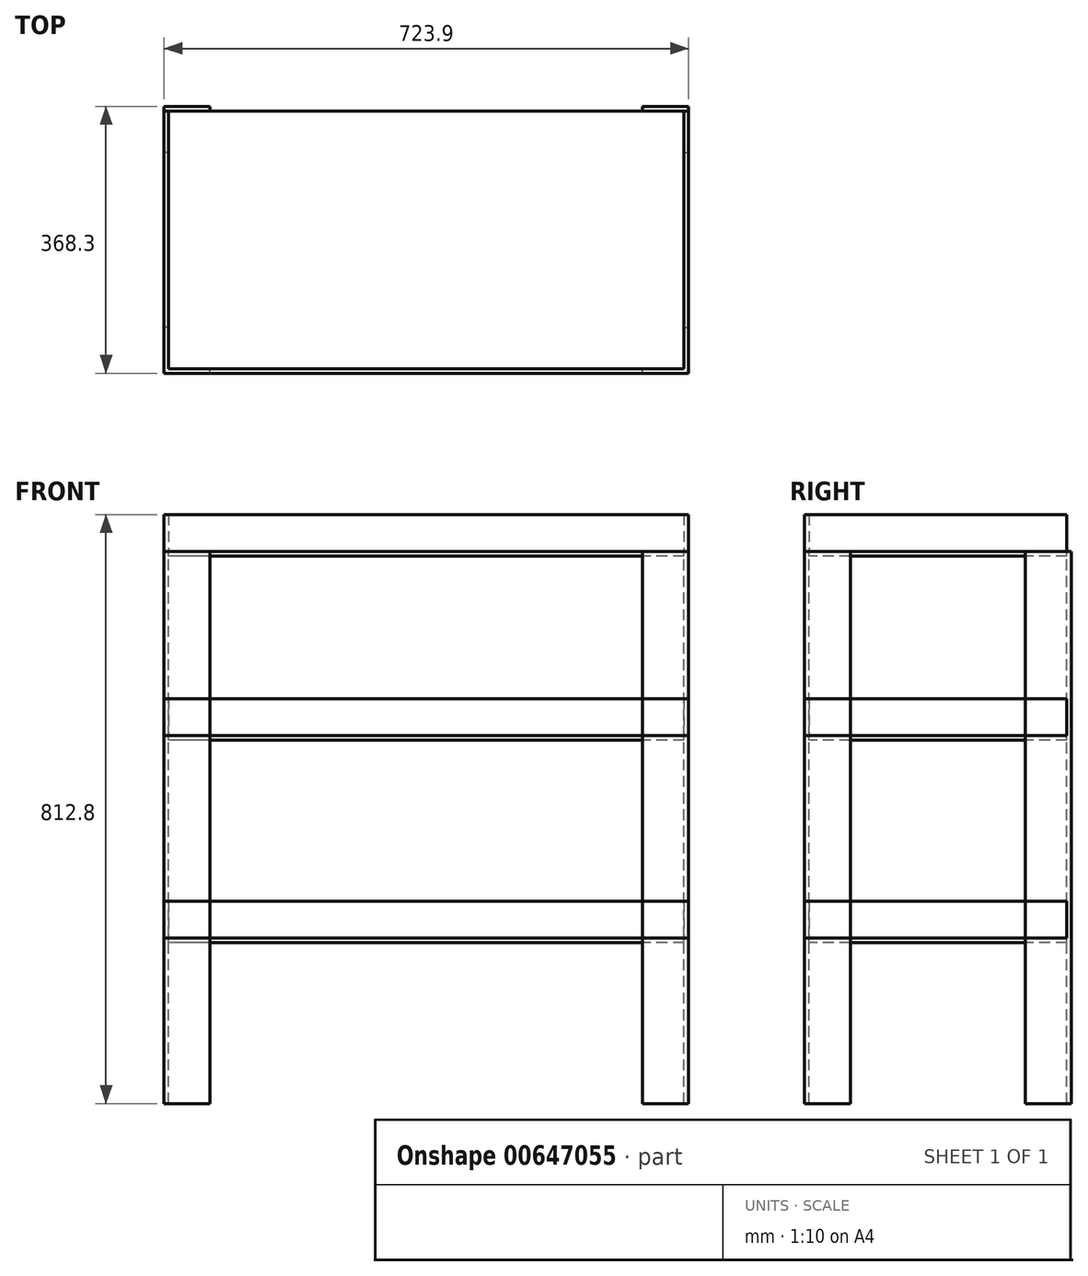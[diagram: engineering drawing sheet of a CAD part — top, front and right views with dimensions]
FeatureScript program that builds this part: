
annotation { "Feature Type Name" : "Feature", "Feature Type Description" : "" }
export const myFeature = defineFeature(function(context is Context, id is Id, definition is map)
    precondition{}
    {
        {
            var Q0;
            Q0=qCreatedBy(makeId("Top.planeOp"),FACE);
            cPlane(context, id + "F0", {"entities" : qUnion([Q0]), "cplaneType" : CPlaneType.OFFSET, "offset" : 152.4 * mm, "width" : 152.4 * mm, "height" : 152.4 * mm});
        }
        {
            var Q0;
            Q0=qCreatedBy(id+"F0.planeOp",FACE);
            cPlane(context, id + "F1", {"entities" : qUnion([Q0]), "cplaneType" : CPlaneType.OFFSET, "offset" : 279.4 * mm, "width" : 152.4 * mm, "height" : 152.4 * mm});
        }
        {
            var Q0;
            Q0=qCreatedBy(id+"F1.planeOp",FACE);
            cPlane(context, id + "F2", {"entities" : qUnion([Q0]), "cplaneType" : CPlaneType.OFFSET, "offset" : 254 * mm, "width" : 152.4 * mm, "height" : 152.4 * mm});
        }
        {
            var Q0;
            Q0=qCreatedBy(id+"F2.planeOp",FACE);
            var sketch = newSketch(context, id + "F3", { "sketchPlane" : qUnion([Q0])});
            skLineSegment(sketch, "E0.bottom", {"start": v(355.6, 177.8) * mm, "end": v(-355.6, 177.8) * mm, "construction": true});
            skLineSegment(sketch, "E0.top", {"start": v(355.6, -177.8) * mm, "end": v(-355.6, -177.8) * mm, "construction": true});
            skLineSegment(sketch, "E0.left", {"start": v(355.6, 177.8) * mm, "end": v(355.6, -177.8) * mm, "construction": true});
            skLineSegment(sketch, "E0.right", {"start": v(-355.6, 177.8) * mm, "end": v(-355.6, -177.8) * mm, "construction": true});
            skPoint(sketch, "E0.middle", {"position": v(0, 0) * mm});
            skLineSegment(sketch, "E1", {"start": v(-355.6, 120.65) * mm, "end": v(-361.95, 120.65) * mm});
            skLineSegment(sketch, "E2", {"start": v(-361.95, 120.65) * mm, "end": v(-361.95, 184.15) * mm});
            skLineSegment(sketch, "E3", {"start": v(-361.95, 184.15) * mm, "end": v(-298.45, 184.15) * mm});
            skLineSegment(sketch, "E4", {"start": v(-298.45, 184.15) * mm, "end": v(-298.45, 177.8) * mm});
            skLineSegment(sketch, "E5", {"start": v(-298.45, 177.8) * mm, "end": v(-355.6, 177.8) * mm});
            skLineSegment(sketch, "E6", {"start": v(-355.6, 120.65) * mm, "end": v(-355.6, 177.8) * mm});
            skLineSegment(sketch, "E7", {"start": v(-355.6, -177.8) * mm, "end": v(-355.6, -120.65) * mm});
            skLineSegment(sketch, "E8", {"start": v(-355.6, -120.65) * mm, "end": v(-361.95, -120.65) * mm});
            skLineSegment(sketch, "E9", {"start": v(-361.95, -184.15) * mm, "end": v(-361.95, -120.65) * mm});
            skLineSegment(sketch, "E10", {"start": v(-361.95, -184.15) * mm, "end": v(-298.45, -184.15) * mm});
            skLineSegment(sketch, "E11", {"start": v(-298.45, -184.15) * mm, "end": v(-298.45, -177.8) * mm});
            skLineSegment(sketch, "E12", {"start": v(-298.45, -177.8) * mm, "end": v(-355.6, -177.8) * mm});
            skLineSegment(sketch, "E13.MirrorCS", {"start": v(361.95, -184.15) * mm, "end": v(298.45, -184.15) * mm});
            skLineSegment(sketch, "E14.MirrorCS", {"start": v(298.45, -177.8) * mm, "end": v(355.6, -177.8) * mm});
            skLineSegment(sketch, "E15.MirrorCS", {"start": v(298.45, -184.15) * mm, "end": v(298.45, -177.8) * mm});
            skLineSegment(sketch, "E16.MirrorCS", {"start": v(355.6, -120.65) * mm, "end": v(361.95, -120.65) * mm});
            skLineSegment(sketch, "E17.MirrorCS", {"start": v(355.6, -177.8) * mm, "end": v(355.6, -120.65) * mm});
            skLineSegment(sketch, "E18.MirrorCS", {"start": v(361.95, -184.15) * mm, "end": v(361.95, -120.65) * mm});
            skLineSegment(sketch, "E19.MirrorCS", {"start": v(355.6, 120.65) * mm, "end": v(355.6, 177.8) * mm});
            skLineSegment(sketch, "E20.MirrorCS", {"start": v(298.45, 177.8) * mm, "end": v(355.6, 177.8) * mm});
            skLineSegment(sketch, "E21.MirrorCS", {"start": v(298.45, 184.15) * mm, "end": v(298.45, 177.8) * mm});
            skLineSegment(sketch, "E22.MirrorCS", {"start": v(361.95, 120.65) * mm, "end": v(361.95, 184.15) * mm});
            skLineSegment(sketch, "E23.MirrorCS", {"start": v(361.95, 184.15) * mm, "end": v(298.45, 184.15) * mm});
            skLineSegment(sketch, "E24.MirrorCS", {"start": v(355.6, 120.65) * mm, "end": v(361.95, 120.65) * mm});
            skLineSegment(sketch, "E25.MirrorCS", {"start": v(-355.6, -177.8) * mm, "end": v(355.6, -177.8) * mm, "construction": true});
            skLineSegment(sketch, "E26.MirrorCS", {"start": v(-355.6, 177.8) * mm, "end": v(355.6, 177.8) * mm, "construction": true});
            skSolve(sketch);
        }
        {
            var Q0;
            Q0 = qSketchRegion(id + "F3", true);
            extrude(context, id + "F4", {"entities" : qUnion([Q0]), "oppositeDirection" : true, "depth" : 762 * mm, "offsetDistance" : 25.4 * mm});
        }
        {
            var Q0;
            Q0=qCreatedBy(id+"F0.planeOp",FACE);
            var sketch = newSketch(context, id + "F5", { "sketchPlane" : qUnion([Q0])});
            skLineSegment(sketch, "E27.bottom", {"start": v(355.6, 177.8) * mm, "end": v(-355.6, 177.8) * mm});
            skLineSegment(sketch, "E27.top", {"start": v(355.6, -177.8) * mm, "end": v(-355.6, -177.8) * mm});
            skLineSegment(sketch, "E27.left", {"start": v(355.6, 177.8) * mm, "end": v(355.6, -177.8) * mm});
            skLineSegment(sketch, "E27.right", {"start": v(-355.6, 177.8) * mm, "end": v(-355.6, -177.8) * mm});
            skPoint(sketch, "E27.middle", {"position": v(0, 0) * mm});
            skSolve(sketch);
        }
        {
            var Q0;
            Q0 = qSketchRegion(id + "F5", true);
            extrude(context, id + "F6", {"entities" : qUnion([Q0]), "oppositeDirection" : true, "depth" : 6.35 * mm, "offsetDistance" : 25.4 * mm});
        }
        {
            var Q0;
            Q0=qCreatedBy(id+"F1.planeOp",FACE);
            var sketch = newSketch(context, id + "F7", { "sketchPlane" : qUnion([Q0])});
            skLineSegment(sketch, "E28.bottom", {"start": v(355.6, 177.8) * mm, "end": v(-355.6, 177.8) * mm});
            skLineSegment(sketch, "E28.top", {"start": v(355.6, -177.8) * mm, "end": v(-355.6, -177.8) * mm});
            skLineSegment(sketch, "E28.left", {"start": v(355.6, 177.8) * mm, "end": v(355.6, -177.8) * mm});
            skLineSegment(sketch, "E28.right", {"start": v(-355.6, 177.8) * mm, "end": v(-355.6, -177.8) * mm});
            skPoint(sketch, "E28.middle", {"position": v(0, 0) * mm});
            skSolve(sketch);
        }
        {
            var Q0;
            Q0 = qSketchRegion(id + "F7", true);
            extrude(context, id + "F8", {"entities" : qUnion([Q0]), "oppositeDirection" : true, "depth" : 6.35 * mm, "offsetDistance" : 25.4 * mm});
        }
        {
            var Q0;
            Q0=qCreatedBy(id+"F2.planeOp",FACE);
            var sketch = newSketch(context, id + "F9", { "sketchPlane" : qUnion([Q0])});
            skLineSegment(sketch, "E29.bottom", {"start": v(355.6, 177.8) * mm, "end": v(-355.6, 177.8) * mm});
            skLineSegment(sketch, "E29.top", {"start": v(355.6, -177.8) * mm, "end": v(-355.6, -177.8) * mm});
            skLineSegment(sketch, "E29.left", {"start": v(355.6, 177.8) * mm, "end": v(355.6, -177.8) * mm});
            skLineSegment(sketch, "E29.right", {"start": v(-355.6, 177.8) * mm, "end": v(-355.6, -177.8) * mm});
            skPoint(sketch, "E29.middle", {"position": v(0, 0) * mm});
            skSolve(sketch);
        }
        {
            var Q0;
            Q0 = qSketchRegion(id + "F9", true);
            extrude(context, id + "F10", {"entities" : qUnion([Q0]), "oppositeDirection" : true, "depth" : 6.35 * mm, "offsetDistance" : 25.4 * mm});
        }
        {
            var Q0;
            Q0=qCreatedBy(id+"F2.planeOp",FACE);
            var sketch = newSketch(context, id + "F11", { "sketchPlane" : qUnion([Q0])});
            skLineSegment(sketch, "E30.bottom", {"start": v(355.6, 177.8) * mm, "end": v(-355.6, 177.8) * mm, "construction": true});
            skLineSegment(sketch, "E30.top", {"start": v(355.6, -177.8) * mm, "end": v(-355.6, -177.8) * mm, "construction": true});
            skLineSegment(sketch, "E30.left", {"start": v(355.6, 177.8) * mm, "end": v(355.6, -177.8) * mm, "construction": true});
            skLineSegment(sketch, "E30.right", {"start": v(-355.6, 177.8) * mm, "end": v(-355.6, -177.8) * mm, "construction": true});
            skPoint(sketch, "E30.middle", {"position": v(0, 0) * mm});
            skLineSegment(sketch, "E31", {"start": v(-355.6, 177.8) * mm, "end": v(-361.95, 177.8) * mm});
            skLineSegment(sketch, "E32", {"start": v(-361.95, 177.8) * mm, "end": v(-361.95, -184.15) * mm});
            skLineSegment(sketch, "E33", {"start": v(-361.95, -184.15) * mm, "end": v(361.95, -184.15) * mm});
            skLineSegment(sketch, "E34", {"start": v(361.95, -184.15) * mm, "end": v(361.95, 177.8) * mm});
            skLineSegment(sketch, "E35", {"start": v(361.95, 177.8) * mm, "end": v(355.6, 177.8) * mm});
            skLineSegment(sketch, "E36", {"start": v(355.6, -177.8) * mm, "end": v(-355.6, -177.8) * mm});
            skLineSegment(sketch, "E37", {"start": v(-355.6, 177.8) * mm, "end": v(-355.6, -177.8) * mm});
            skLineSegment(sketch, "E38", {"start": v(-355.6, -177.8) * mm, "end": v(355.6, -177.8) * mm});
            skLineSegment(sketch, "E39", {"start": v(355.6, -177.8) * mm, "end": v(355.6, 177.8) * mm});
            skSolve(sketch);
        }
        {
            var Q0;
            Q0 = qSketchRegion(id + "F11", true);
            extrude(context, id + "F12", {"entities" : qUnion([Q0]), "depth" : 50.8 * mm, "offsetDistance" : 25.4 * mm});
        }
        {
            var Q0;
            Q0=qCreatedBy(id+"F1.planeOp",FACE);
            var sketch = newSketch(context, id + "F13", { "sketchPlane" : qUnion([Q0])});
            skLineSegment(sketch, "E40.bottom", {"start": v(355.6, 177.8) * mm, "end": v(-355.6, 177.8) * mm, "construction": true});
            skLineSegment(sketch, "E40.top", {"start": v(355.6, -177.8) * mm, "end": v(-355.6, -177.8) * mm, "construction": true});
            skLineSegment(sketch, "E40.left", {"start": v(355.6, 177.8) * mm, "end": v(355.6, -177.8) * mm, "construction": true});
            skLineSegment(sketch, "E40.right", {"start": v(-355.6, 177.8) * mm, "end": v(-355.6, -177.8) * mm, "construction": true});
            skPoint(sketch, "E40.middle", {"position": v(0, 0) * mm});
            skLineSegment(sketch, "E41", {"start": v(-355.6, 177.8) * mm, "end": v(-361.95, 177.8) * mm});
            skLineSegment(sketch, "E42", {"start": v(-361.95, 177.8) * mm, "end": v(-361.95, -184.15) * mm});
            skLineSegment(sketch, "E43", {"start": v(-361.95, -184.15) * mm, "end": v(361.95, -184.15) * mm});
            skLineSegment(sketch, "E44", {"start": v(361.95, -184.15) * mm, "end": v(361.95, 177.8) * mm});
            skLineSegment(sketch, "E45", {"start": v(361.95, 177.8) * mm, "end": v(355.6, 177.8) * mm});
            skLineSegment(sketch, "E46", {"start": v(355.6, 177.8) * mm, "end": v(355.6, -177.8) * mm});
            skLineSegment(sketch, "E47", {"start": v(355.6, -177.8) * mm, "end": v(-355.6, -177.8) * mm});
            skLineSegment(sketch, "E48", {"start": v(-355.6, -177.8) * mm, "end": v(-355.6, 177.8) * mm});
            skSolve(sketch);
        }
        {
            var Q0;
            Q0 = qSketchRegion(id + "F13", true);
            extrude(context, id + "F14", {"entities" : qUnion([Q0]), "depth" : 50.8 * mm, "offsetDistance" : 25.4 * mm});
        }
        {
            var Q0;
            Q0=qCreatedBy(id+"F0.planeOp",FACE);
            var sketch = newSketch(context, id + "F15", { "sketchPlane" : qUnion([Q0])});
            skLineSegment(sketch, "E49.bottom", {"start": v(355.6, 177.8) * mm, "end": v(-355.6, 177.8) * mm, "construction": true});
            skLineSegment(sketch, "E49.top", {"start": v(355.6, -177.8) * mm, "end": v(-355.6, -177.8) * mm, "construction": true});
            skLineSegment(sketch, "E49.left", {"start": v(355.6, 177.8) * mm, "end": v(355.6, -177.8) * mm, "construction": true});
            skLineSegment(sketch, "E49.right", {"start": v(-355.6, 177.8) * mm, "end": v(-355.6, -177.8) * mm, "construction": true});
            skPoint(sketch, "E49.middle", {"position": v(0, 0) * mm});
            skLineSegment(sketch, "E50", {"start": v(-355.6, 177.8) * mm, "end": v(-361.95, 177.8) * mm});
            skLineSegment(sketch, "E51", {"start": v(-361.95, 177.8) * mm, "end": v(-361.95, -184.15) * mm});
            skLineSegment(sketch, "E52", {"start": v(-361.95, -184.15) * mm, "end": v(361.95, -184.15) * mm});
            skLineSegment(sketch, "E53", {"start": v(361.95, -184.15) * mm, "end": v(361.95, 177.8) * mm});
            skLineSegment(sketch, "E54", {"start": v(361.95, 177.8) * mm, "end": v(355.6, 177.8) * mm});
            skLineSegment(sketch, "E55", {"start": v(355.6, 177.8) * mm, "end": v(355.6, -177.8) * mm});
            skLineSegment(sketch, "E56", {"start": v(355.6, -177.8) * mm, "end": v(-355.6, -177.8) * mm});
            skLineSegment(sketch, "E57", {"start": v(-355.6, -177.8) * mm, "end": v(-355.6, 177.8) * mm});
            skSolve(sketch);
        }
        {
            var Q0;
            Q0 = qSketchRegion(id + "F15", true);
            extrude(context, id + "F16", {"entities" : qUnion([Q0]), "depth" : 50.8 * mm, "offsetDistance" : 25.4 * mm});
        }
    });
